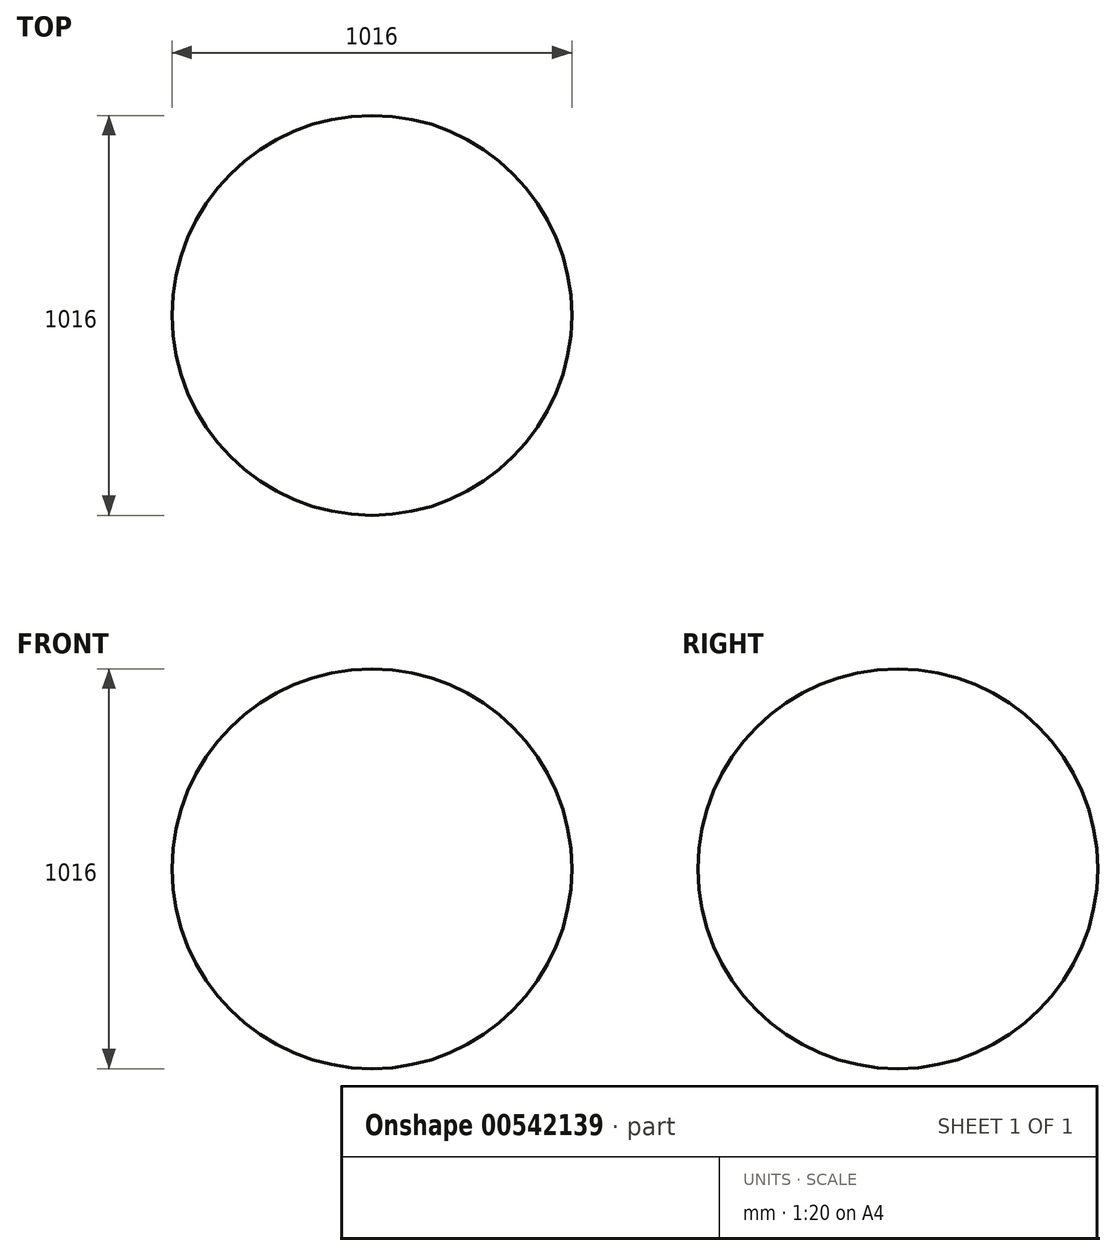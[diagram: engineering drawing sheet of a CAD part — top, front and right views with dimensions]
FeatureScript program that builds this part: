
annotation { "Feature Type Name" : "Feature", "Feature Type Description" : "" }
export const myFeature = defineFeature(function(context is Context, id is Id, definition is map)
    precondition{}
    {
        {
            var Q0;
            Q0=qCreatedBy(makeId("Front.planeOp"),FACE);
            var sketch = newSketch(context, id + "F0", { "sketchPlane" : qUnion([Q0])});
            skArc(sketch, "E0", {"start": v(0, 508) * mm, "mid": v(-508, 0) * mm, "end": v(0, -508) * mm});
            skLineSegment(sketch, "E1", {"start": v(0, 508) * mm, "end": v(0, -508) * mm});
            skSolve(sketch);
        }
        {
            var Q0;
            Q0=qSketchRegion(id+"F0",true);
            var Q1;
            Q1=sQuery(id+"F0.wireOp",EDGE,"E1");
            revolve(context, id + "F1", {"entities" : qUnion([Q0]), "axis" : qUnion([Q1]), "revolveType" : RevolveType.FULL});
        }
    });
